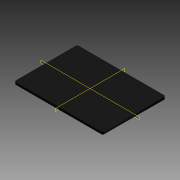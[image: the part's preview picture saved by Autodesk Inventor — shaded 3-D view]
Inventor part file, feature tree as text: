
AUTODESK INVENTOR PART (.ipt)
format: ipt  version: 2015 (Build 190159000, 159)  size: 128,000 bytes
history: native  units: mm
features: extrude x4, fillet x1, other x1
ambient origin geometry x8: Origin, YZ Plane, XZ Plane, XY Plane, X Axis, Y Axis, Z Axis, Center Point
bodies: Solid1 (feature_tree)
feature tree (6):
  extrude  "Extrusión1"  Depth=305.3mm
  fillet  "Empalme1"  Radius=217.0mm
  extrude  "Limites"  Depth=8.0mm TaperAngle=0.0deg
  extrude  "Extrusión3"  Depth=5.0mm
  other  "POSICION IMANES"
  extrude  "Extrusión4"  Depth=297.0mm
